# Revit family: 7212_Tosca
name_source: partatom
category: Lighting Fixtures
revit_build: Autodesk Revit LT 2016 (Build: 20150220_1215(x64)
units: mm (PartAtom-declared; Revit-internal decimal feet)

## family parameters
Cut with Voids When Loaded = No
Host = Face
Light Source = No
OmniClass Number = 23.80.70.00
OmniClass Title = Lighting
Part Type = Normal
Room Calculation Point = No
Round Connector Dimension = Use Diameter
Shared = No

## types (3) — shared parameters
Apparent Load = 2 VA
Arm Length = 6.27 "
Assembly Code = D5020200
Class = 1
Description = Wall Reading Light
Dimmable = No
Height = 1.77 "
IP Rating = IP20
Lamp = LED
Lamp included = Yes
Length = 1.68 "
Lens Material = Astro - Glass - Clear
Location = DRY
Luminaire Lamp Efficiency Rating = A
Manufacturer = Astro Lighting Ltd, CM20 2DP
Mountable on normally flammable surfaces = Yes
Number of Poles = 1
Product Documentation = https://www.astrolighting.com
Type Comments = Includes integral LED driver. Includes integral switch.
URL = www.astrolighting.co.uk
Voltage = 240 V
Voltage Range = 100-240V
Wattage Comments = 1w
Weight = 1.2kg
Width = 7.87 "

## per-type parameters (varying)
| type | Casing Material | Model |
| 7213 Tosca (Brushed Matt Nickel) | Astro - Steel - Matt Nickel | 7213 Tosca Brushed Matt Nickel |
| 7214 Tosca (Brushed Bronze) | Astro - Steel - Bronze | 7214 Tosca Brushed Bronze |
| 7212 Tosca (Polished Chrome) | Astro - Steel - Chrome Finish | 7212 Tosca Polished Chrome |

## geometry (parser evidence)
native form markers: Sweep x7
no freeform markers — native parametric forms only
